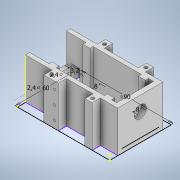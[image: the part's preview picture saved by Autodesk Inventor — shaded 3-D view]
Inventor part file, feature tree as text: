
AUTODESK INVENTOR PART (.ipt)
format: ipt  version: 2020.3 (Build 243373000, 373)  size: 502,272 bytes
history: native  units: mm
features: extrude x12, sketch x9
ambient origin geometry x8: Origin, YZ Plane, XZ Plane, XY Plane, X Axis, Y Axis, Z Axis, Center Point
bodies: Solid1 (feature_tree)
feature tree (21):
  sketch  "Sketch1"  dims[d0=90.0mm d1=60.0mm]
  extrude  "Extrusion1"  Depth=60.0mm
  extrude  "Extrusion2"  Depth=40.0mm TaperAngle=0.0deg
  extrude  "Extrusion3"  Depth=3.2mm
  extrude  "Extrusion4"  Depth=3.2mm
  sketch  "Sketch4"  dims[d9=3.2mm d10=3.2mm]
  extrude  "Extrusion5"  Depth=2.0mm
  extrude  "Extrusion6"  Depth=30.0mm
  extrude  "Extrusion7"  Depth=36.0mm TaperAngle=0.0deg
  extrude  "Extrusion8"  Depth=20.0mm TaperAngle=0.0deg
  extrude  "Extrusion9"  Depth=4.0mm TaperAngle=0.0deg
  sketch  "Sketch8"  dims[d18=36.0mm d19=0.0mm d20=36.0mm d21=0.0mm]
  extrude  "Extrusion14"  Depth=15.0mm TaperAngle=0.0deg
  extrude  "Extrusion15"  Depth=15.0mm TaperAngle=0.0deg
  extrude  "Extrusion16"  Depth=8.0mm
  sketch  "Sketch10"  dims[d30=20.0mm d31=4.0mm d32=0.0mm d41=15.0mm d42=0.0mm d43=15.0mm d44=0.0mm d45=11.5mm d46=2.0mm d47=10.0mm d48=0.0mm d49=8.0mm d50=8.0mm d51=2.4mm d54=2.4mm]
  sketch  "Sketch2"  dims[d2=4.0mm d3=0.0mm d4=40.0mm d5=0.0mm]
  sketch  "Sketch3"  dims[d6=3.2mm d7=3.2mm]
  sketch  "Sketch5"  dims[d11=100.0mm d12=0.0mm d13=2.0mm]
  sketch  "Sketch6"  dims[d14=30.0mm d15=0.0mm d16=3.2mm]
  sketch  "Sketch9"  dims[d22=1.0mm d23=0.0mm d25=20.0mm d26=0.0mm]
